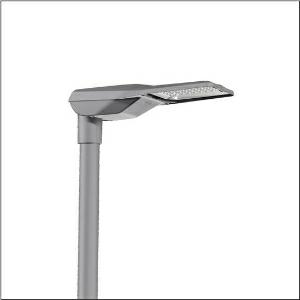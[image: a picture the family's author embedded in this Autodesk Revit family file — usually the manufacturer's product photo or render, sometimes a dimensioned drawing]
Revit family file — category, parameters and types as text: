
# Revit family: streetlight_sl_21_iq_mini___p1_0a_5xe2a41g08gb_a1a0
name_source: partatom
category: Lighting Fixtures
units: mm (PartAtom-declared; Revit-internal decimal feet)

## family parameters
Cut with Voids When Loaded = No
Host = Face
Light Source = No
Part Type = Normal
Room Calculation Point = No
Round Connector Dimension = Use Diameter
Shared = No

## types (1)
- --- (1 x LED, 5920 lm, 37.1 W, 4000K)
    Apparent Load = 37 VA
    CIE Flux Codes = 21 50 90 100 100
    Color Rendering = 70
    Color Temperature = 4000K
    Default Elevation = 1800 mm
    Description = Streetlight SL 21 mini, mast luminaire, primary light control with lens, of PMMA, primary optical cover: cover, of toughened safety glass, transparent, light distribution: P1.0a, light emission: direct distribution, primary light characteristic: asymmetric, installation type: post-top, side-entry, LED, High Power LED, rated luminous flux: 5.920lm, luminous efficacy: 160lm/W, light colour: 740, colour temperature: 4000K, control gear: ECG iQ, control: Street-Remote, Auto-Match, Temp-Guard, Lumen-Switch, Night-Set, Smart-Wire, Light-Fading, Desk-Remote (wireless, voltage-free reading and setting of iQ features in the workshop via application-optimized NFC function/RFID function), optimised constant luminous flux control (CLO 2.0), mains connection: 220..240V, AC, 50/60Hz, start of lifetime: 37W, end of lifetime: 39W, reduction: 18W, luminaire housing, of diecast aluminium, powder-coated, Siteco® metallic grey (DB 702S), corrosivity category C5 according to DIN EN ISO 12944, length: 628mm, width: 235mm, height: 110mm, spigot size: 60/76mm (post-top) and 42/60/76mm (side-entry), mast flange for spigot size: 42mm: 5XC10008XM4, 60mm: 5XC10008XM2, 76/60mm: 5XC10108XM1, protection rating (complete): IP66, insulation class (complete): insulation class II (safety insulation), certification: CE, ENEC, VDE, impact resistance: IK09, permissible operating ambient temperature for outdoor applications: -40..+50°C, standard-compliant lighting for roads and squares, packaging unit: 1 piece

Light Distribution: P1.0a
    Height = 110 mm
    Lamp = 1 x LED
    Lamp Light Flux = 5920 lm
    Lamp Power = 37.1 W
    Lamp count = 1
    Length = 625 mm
    Luminous efficacy = 160 lm/W
    Manufacturer = Siteco
    ModVariant = No
    Model = 5XE2A41G08GB
    Number of Poles = 1
    OnlyDefault = Yes
    Power Factor = 1
    Product Name = Streetlight SL 21 iQ mini | P1.0a
    Product group = mast luminaire | pylon top
    ProductGroupID = 6100
    Protection Class = Protection class II
    Protection Degree = IP 66
    RLX_Detail_Level = 1
    RlxData = <blob elided: 103309 chars, md5=3e78932a>
    Socket = socket
    Standby Power = 0 W
    System Light Flux = 5920 lm
    System Power = 37 W
    Type Comments = factory setting: luminous flux: 100 % | dim-lin: 254 | 385 mA
    Type Image = l_1003519.jpg
    URL = http://relux.com
    VarID = @adj_103811
    Voltage = 0 V
    Weight = 0.00 kg
    Width = 234 mm

## geometry (parser evidence)
native form markers: Blend x4, Sweep x9
no freeform markers — native parametric forms only
